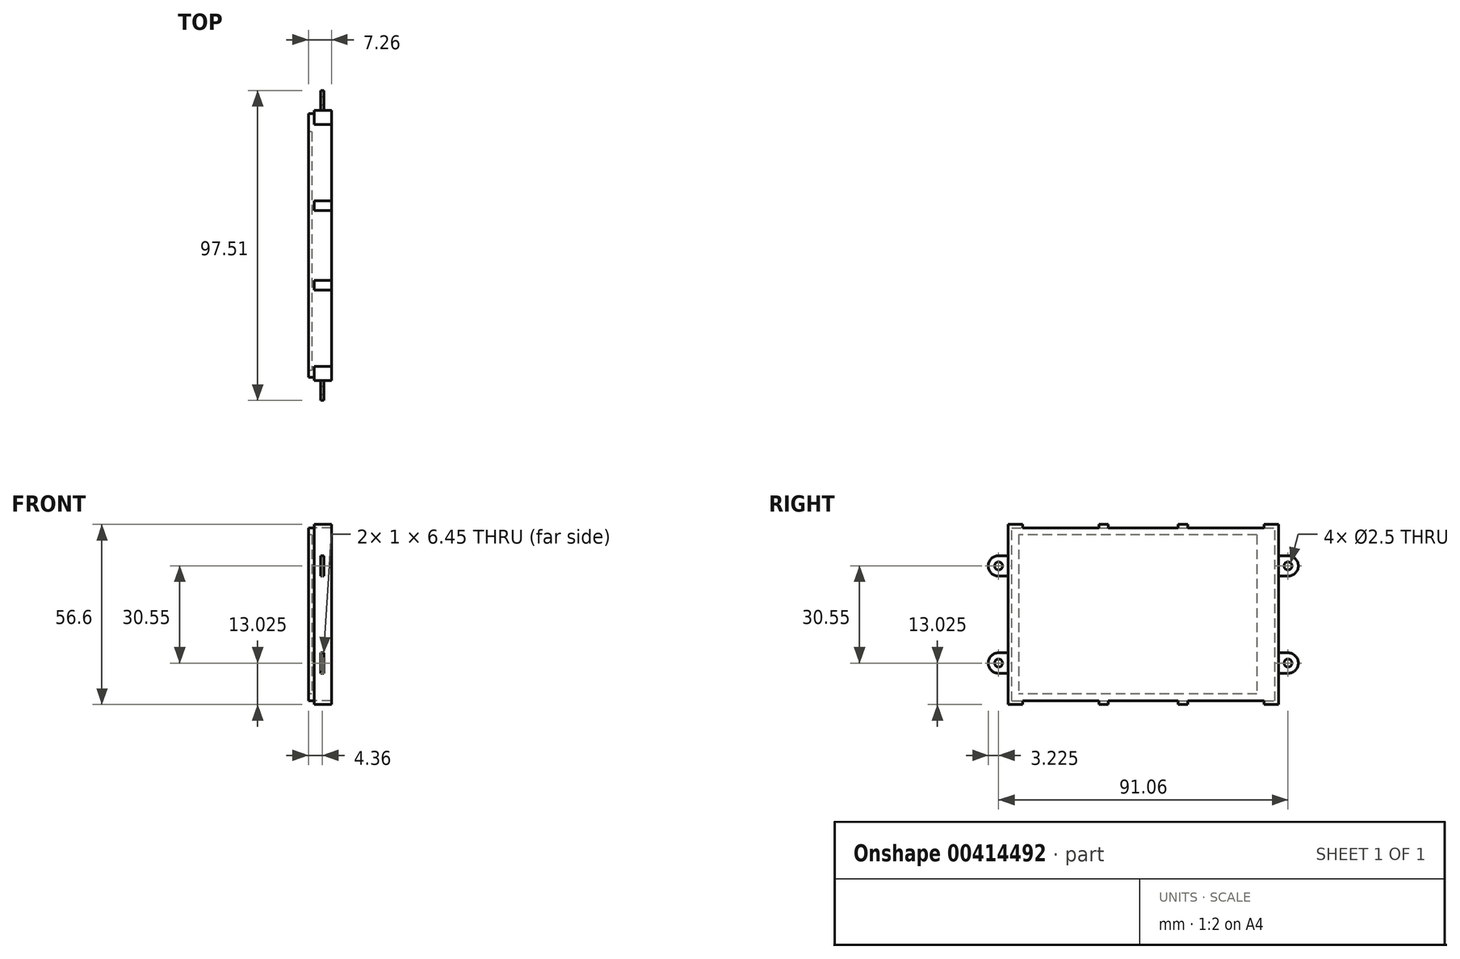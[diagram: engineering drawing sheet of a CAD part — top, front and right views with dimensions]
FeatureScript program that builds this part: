
annotation { "Feature Type Name" : "Feature", "Feature Type Description" : "" }
export const myFeature = defineFeature(function(context is Context, id is Id, definition is map)
    precondition{}
    {
        {
            var Q0;
            Q0=qCreatedBy(makeId("Right.planeOp"),FACE);
            var sketch = newSketch(context, id + "F0", { "sketchPlane" : qUnion([Q0])});
            skLineSegment(sketch, "E0.bottom", {"start": v(0, 0) * mm, "end": v(82.87, 0) * mm});
            skLineSegment(sketch, "E0.top", {"start": v(0, 54.4) * mm, "end": v(82.87, 54.4) * mm});
            skLineSegment(sketch, "E0.left", {"start": v(0, 0) * mm, "end": v(0, 54.4) * mm});
            skLineSegment(sketch, "E0.right", {"start": v(82.87, 0) * mm, "end": v(82.87, 54.4) * mm});
            skSolve(sketch);
        }
        {
            var Q0;
            Q0=makeQuery(id+"F0.imprint","IMPRINT",FACE,{"disambiguationData":[TD([[makeQuery(id+"F0.imprint","IMPRINT",EDGE,{"derivedFrom":sQuery(id+"F0.wireOp",EDGE,"E0.bottom")}),1.0]])]});
            extrude(context, id + "F1", {"entities" : qUnion([Q0]), "depth" : 1.76 * mm, "offsetDistance" : 25 * mm});
        }
        {
            var Q0;
            Q0=makeQuery(id+"F1.opExtrude","CAP_FACE",FACE,{"disambiguationData":[OSD([sQuery(id+"F0.wireOp",EDGE,"E0.bottom"),sQuery(id+"F0.wireOp",EDGE,"E0.top"),sQuery(id+"F0.wireOp",EDGE,"E0.left"),sQuery(id+"F0.wireOp",EDGE,"E0.right")])],"isStart":false});
            var sketch = newSketch(context, id + "F2", { "sketchPlane" : qUnion([Q0])});
            skLineSegment(sketch, "E1.bottom", {"start": v(0, 0) * mm, "end": v(82.87, 0) * mm});
            skLineSegment(sketch, "E1.top", {"start": v(0, 54.4) * mm, "end": v(82.87, 54.4) * mm});
            skLineSegment(sketch, "E1.left", {"start": v(0, 0) * mm, "end": v(0, 54.4) * mm});
            skLineSegment(sketch, "E1.right", {"start": v(82.87, 0) * mm, "end": v(82.87, 54.4) * mm});
            skLineSegment(sketch, "E2.bottom", {"start": v(79.42, 55.5) * mm, "end": v(83.97, 55.5) * mm});
            skLineSegment(sketch, "E2.top", {"start": v(79.42, -1.1) * mm, "end": v(83.97, -1.1) * mm});
            skLineSegment(sketch, "E2.left", {"start": v(79.42, 55.5) * mm, "end": v(79.42, 54.4) * mm});
            skLineSegment(sketch, "E2.right", {"start": v(83.97, 55.5) * mm, "end": v(83.97, -1.1) * mm});
            skLineSegment(sketch, "E3.bottom", {"start": v(-1.1, 55.5) * mm, "end": v(3.45, 55.5) * mm});
            skLineSegment(sketch, "E3.top", {"start": v(-1.1, -1.1) * mm, "end": v(3.45, -1.1) * mm});
            skLineSegment(sketch, "E3.left", {"start": v(-1.1, 55.5) * mm, "end": v(-1.1, -1.1) * mm});
            skLineSegment(sketch, "E3.right", {"start": v(3.45, 55.5) * mm, "end": v(3.45, 54.4) * mm});
            skLineSegment(sketch, "E4.bottom", {"start": v(27.45, 55.5) * mm, "end": v(30.47, 55.5) * mm});
            skLineSegment(sketch, "E4.top", {"start": v(27.45, -1.1) * mm, "end": v(30.47, -1.1) * mm});
            skLineSegment(sketch, "E4.left", {"start": v(27.45, 55.5) * mm, "end": v(27.45, 54.4) * mm});
            skLineSegment(sketch, "E4.right", {"start": v(30.47, 55.5) * mm, "end": v(30.47, 54.4) * mm});
            skLineSegment(sketch, "E5.bottom", {"start": v(52.4, 55.5) * mm, "end": v(55.42, 55.5) * mm});
            skLineSegment(sketch, "E5.top", {"start": v(52.4, -1.1) * mm, "end": v(55.42, -1.1) * mm});
            skLineSegment(sketch, "E5.left", {"start": v(52.4, 55.5) * mm, "end": v(52.4, 54.4) * mm});
            skLineSegment(sketch, "E5.right", {"start": v(55.42, 55.5) * mm, "end": v(55.42, 54.4) * mm});
            skLineSegment(sketch, "E6", {"start": v(-19.42, 55.5) * mm, "end": v(99.5, 55.5) * mm, "construction": true});
            skLineSegment(sketch, "E7.trimOffspring", {"start": v(3.45, 0) * mm, "end": v(3.45, -1.1) * mm});
            skLineSegment(sketch, "E8.trimOffspring", {"start": v(27.45, 0) * mm, "end": v(27.45, -1.1) * mm});
            skLineSegment(sketch, "E9.trimOffspring", {"start": v(30.47, 0) * mm, "end": v(30.47, -1.1) * mm});
            skLineSegment(sketch, "E10.trimOffspring", {"start": v(52.4, 0) * mm, "end": v(52.4, -1.1) * mm});
            skLineSegment(sketch, "E11.trimOffspring", {"start": v(55.42, 0) * mm, "end": v(55.42, -1.1) * mm});
            skLineSegment(sketch, "E12.trimOffspring", {"start": v(79.42, 0) * mm, "end": v(79.42, -1.1) * mm});
            skSolve(sketch);
        }
        {
            var Q0;
            Q0 = qSketchRegion(id + "F2", true);
            extrude(context, id + "F3", {"entities" : qUnion([Q0]), "operationType" : NewBodyOperationType.ADD, "depth" : 5.5 * mm, "offsetDistance" : 25 * mm});
        }
        {
            var Q0;
            Q0=makeQuery(id+"F3.opExtrude","CAP_FACE",FACE,{"disambiguationData":[OSD([sQuery(id+"F2.wireOp",EDGE,"E1.bottom"),sQuery(id+"F2.wireOp",EDGE,"E1.top"),sQuery(id+"F2.wireOp",EDGE,"E2.bottom"),sQuery(id+"F2.wireOp",EDGE,"E2.top"),sQuery(id+"F2.wireOp",EDGE,"E2.left"),sQuery(id+"F2.wireOp",EDGE,"E2.right"),sQuery(id+"F2.wireOp",EDGE,"E3.bottom"),sQuery(id+"F2.wireOp",EDGE,"E3.top"),sQuery(id+"F2.wireOp",EDGE,"E3.left"),sQuery(id+"F2.wireOp",EDGE,"E3.right"),sQuery(id+"F2.wireOp",EDGE,"E4.bottom"),sQuery(id+"F2.wireOp",EDGE,"E4.top"),sQuery(id+"F2.wireOp",EDGE,"E4.left"),sQuery(id+"F2.wireOp",EDGE,"E4.right"),sQuery(id+"F2.wireOp",EDGE,"E5.bottom"),sQuery(id+"F2.wireOp",EDGE,"E5.top"),sQuery(id+"F2.wireOp",EDGE,"E5.left"),sQuery(id+"F2.wireOp",EDGE,"E5.right"),sQuery(id+"F2.wireOp",EDGE,"E7.trimOffspring"),sQuery(id+"F2.wireOp",EDGE,"E8.trimOffspring"),sQuery(id+"F2.wireOp",EDGE,"E9.trimOffspring"),sQuery(id+"F2.wireOp",EDGE,"E10.trimOffspring"),sQuery(id+"F2.wireOp",EDGE,"E11.trimOffspring"),sQuery(id+"F2.wireOp",EDGE,"E12.trimOffspring")])],"isStart":false});
            cPlane(context, id + "F4", {"entities" : qUnion([Q0]), "cplaneType" : CPlaneType.OFFSET, "offset" : 2.4 * mm, "oppositeDirection" : true, "width" : 150 * mm, "height" : 150 * mm});
        }
        {
            var Q0;
            Q0=qCreatedBy(id+"F4.planeOp",FACE);
            var sketch = newSketch(context, id + "F5", { "sketchPlane" : qUnion([Q0])});
            skCircle(sketch, "E13", {"center": v(86.97, 11.93) * mm, "radius": 3.23 * mm});
            skCircle(sketch, "E14", {"center": v(86.97, 11.93) * mm, "radius": 1.25 * mm});
            skLineSegment(sketch, "E15.bottom", {"start": v(83.97, 15.15) * mm, "end": v(86.97, 15.15) * mm});
            skLineSegment(sketch, "E15.top", {"start": v(83.97, 8.7) * mm, "end": v(86.97, 8.7) * mm});
            skLineSegment(sketch, "E15.left", {"start": v(83.97, 15.15) * mm, "end": v(83.97, 8.7) * mm});
            skLineSegment(sketch, "E15.right", {"start": v(86.97, 15.15) * mm, "end": v(86.97, 8.7) * mm, "construction": true});
            skCircle(sketch, "E16", {"center": v(86.97, 42.48) * mm, "radius": 3.23 * mm});
            skCircle(sketch, "E17", {"center": v(86.97, 42.48) * mm, "radius": 1.25 * mm});
            skLineSegment(sketch, "E18.bottom", {"start": v(83.97, 45.7) * mm, "end": v(86.97, 45.7) * mm});
            skLineSegment(sketch, "E18.top", {"start": v(83.97, 39.25) * mm, "end": v(86.97, 39.25) * mm});
            skLineSegment(sketch, "E18.left", {"start": v(83.97, 45.7) * mm, "end": v(83.97, 39.25) * mm});
            skLineSegment(sketch, "E18.right", {"start": v(86.97, 45.7) * mm, "end": v(86.97, 39.25) * mm, "construction": true});
            skLineSegment(sketch, "E19", {"start": v(41.44, 57.9) * mm, "end": v(41.44, -8.76) * mm, "construction": true});
            skLineSegment(sketch, "E20.MirrorCS", {"start": v(-1.1, 45.7) * mm, "end": v(-4.1, 45.7) * mm});
            skLineSegment(sketch, "E21.MirrorCS", {"start": v(-4.1, 45.7) * mm, "end": v(-4.1, 39.25) * mm, "construction": true});
            skLineSegment(sketch, "E22.MirrorCS", {"start": v(-4.1, 15.15) * mm, "end": v(-4.1, 8.7) * mm, "construction": true});
            skLineSegment(sketch, "E23.MirrorCS", {"start": v(-1.1, 8.7) * mm, "end": v(-4.1, 8.7) * mm});
            skLineSegment(sketch, "E24.MirrorCS", {"start": v(-1.1, 15.15) * mm, "end": v(-4.1, 15.15) * mm});
            skLineSegment(sketch, "E25.MirrorCS", {"start": v(-1.1, 39.25) * mm, "end": v(-4.1, 39.25) * mm});
            skLineSegment(sketch, "E26.MirrorCS", {"start": v(-1.1, 45.7) * mm, "end": v(-1.1, 39.25) * mm});
            skCircle(sketch, "E27.MirrorC", {"center": v(-4.1, 42.48) * mm, "radius": 1.25 * mm});
            skCircle(sketch, "E28.MirrorC", {"center": v(-4.1, 42.48) * mm, "radius": 3.23 * mm});
            skCircle(sketch, "E29.MirrorC", {"center": v(-4.1, 11.92) * mm, "radius": 3.23 * mm});
            skLineSegment(sketch, "E30.MirrorCS", {"start": v(-1.1, 15.15) * mm, "end": v(-1.1, 8.7) * mm});
            skCircle(sketch, "E31.MirrorC", {"center": v(-4.1, 11.92) * mm, "radius": 1.25 * mm});
            skSolve(sketch);
        }
        {
            var Q0;
            Q0 = qSketchRegion(id + "F5", true);
            extrude(context, id + "F6", {"entities" : qUnion([Q0]), "operationType" : NewBodyOperationType.ADD, "oppositeDirection" : true, "depth" : 1 * mm, "offsetDistance" : 25 * mm});
        }
        {
            var Q0;
            Q0=makeQuery(id+"F1.opExtrude","CAP_FACE",FACE,{"disambiguationData":[OSD([sQuery(id+"F0.wireOp",EDGE,"E0.bottom"),sQuery(id+"F0.wireOp",EDGE,"E0.top"),sQuery(id+"F0.wireOp",EDGE,"E0.left"),sQuery(id+"F0.wireOp",EDGE,"E0.right")])],"isStart":true});
            var sketch = newSketch(context, id + "F7", { "sketchPlane" : qUnion([Q0])});
            skLineSegment(sketch, "E32.bottom", {"start": v(-77.17, 52.2) * mm, "end": v(-2.17, 52.2) * mm});
            skLineSegment(sketch, "E32.top", {"start": v(-77.17, 2.2) * mm, "end": v(-2.17, 2.2) * mm});
            skLineSegment(sketch, "E32.left", {"start": v(-77.17, 52.2) * mm, "end": v(-77.17, 2.2) * mm});
            skLineSegment(sketch, "E32.right", {"start": v(-2.17, 52.2) * mm, "end": v(-2.17, 2.2) * mm});
            skLineSegment(sketch, "E33", {"start": v(-82.87, 27.2) * mm, "end": v(0, 27.2) * mm, "construction": true});
            skLineSegment(sketch, "E34", {"start": v(-41.44, 54.4) * mm, "end": v(-41.44, 0) * mm, "construction": true});
            skSolve(sketch);
        }
        {
            var Q0;
            Q0 = qSketchRegion(id + "F7", true);
            extrude(context, id + "F8", {"entities" : qUnion([Q0]), "operationType" : NewBodyOperationType.REMOVE, "oppositeDirection" : true, "depth" : 1 * mm, "offsetDistance" : 25 * mm});
        }
        {
            var Q0;
            Q0=makeQuery(id+"F8.boolean.opBoolean","COPY",FACE,{"derivedFrom":makeQuery(id+"F8.opExtrude","CAP_FACE",FACE,{"disambiguationData":[OSD([sQuery(id+"F7.wireOp",EDGE,"E32.bottom"),sQuery(id+"F7.wireOp",EDGE,"E32.top"),sQuery(id+"F7.wireOp",EDGE,"E32.left"),sQuery(id+"F7.wireOp",EDGE,"E32.right")])],"isStart":false})});
            var sketch = newSketch(context, id + "F9", { "sketchPlane" : qUnion([Q0])});
            skLineSegment(sketch, "E35.bottom", {"start": v(-77.17, 52.2) * mm, "end": v(-2.17, 52.2) * mm});
            skLineSegment(sketch, "E35.top", {"start": v(-77.17, 2.2) * mm, "end": v(-2.17, 2.2) * mm});
            skLineSegment(sketch, "E35.left", {"start": v(-77.17, 52.2) * mm, "end": v(-77.17, 2.2) * mm});
            skLineSegment(sketch, "E35.right", {"start": v(-2.17, 52.2) * mm, "end": v(-2.17, 2.2) * mm});
            skSolve(sketch);
        }
        {
            var Q0;
            Q0 = qSketchRegion(id + "F9", true);
            extrude(context, id + "F10", {"entities" : qUnion([Q0]), "depth" : 1 * mm, "offsetDistance" : 25 * mm});
        }
    });
